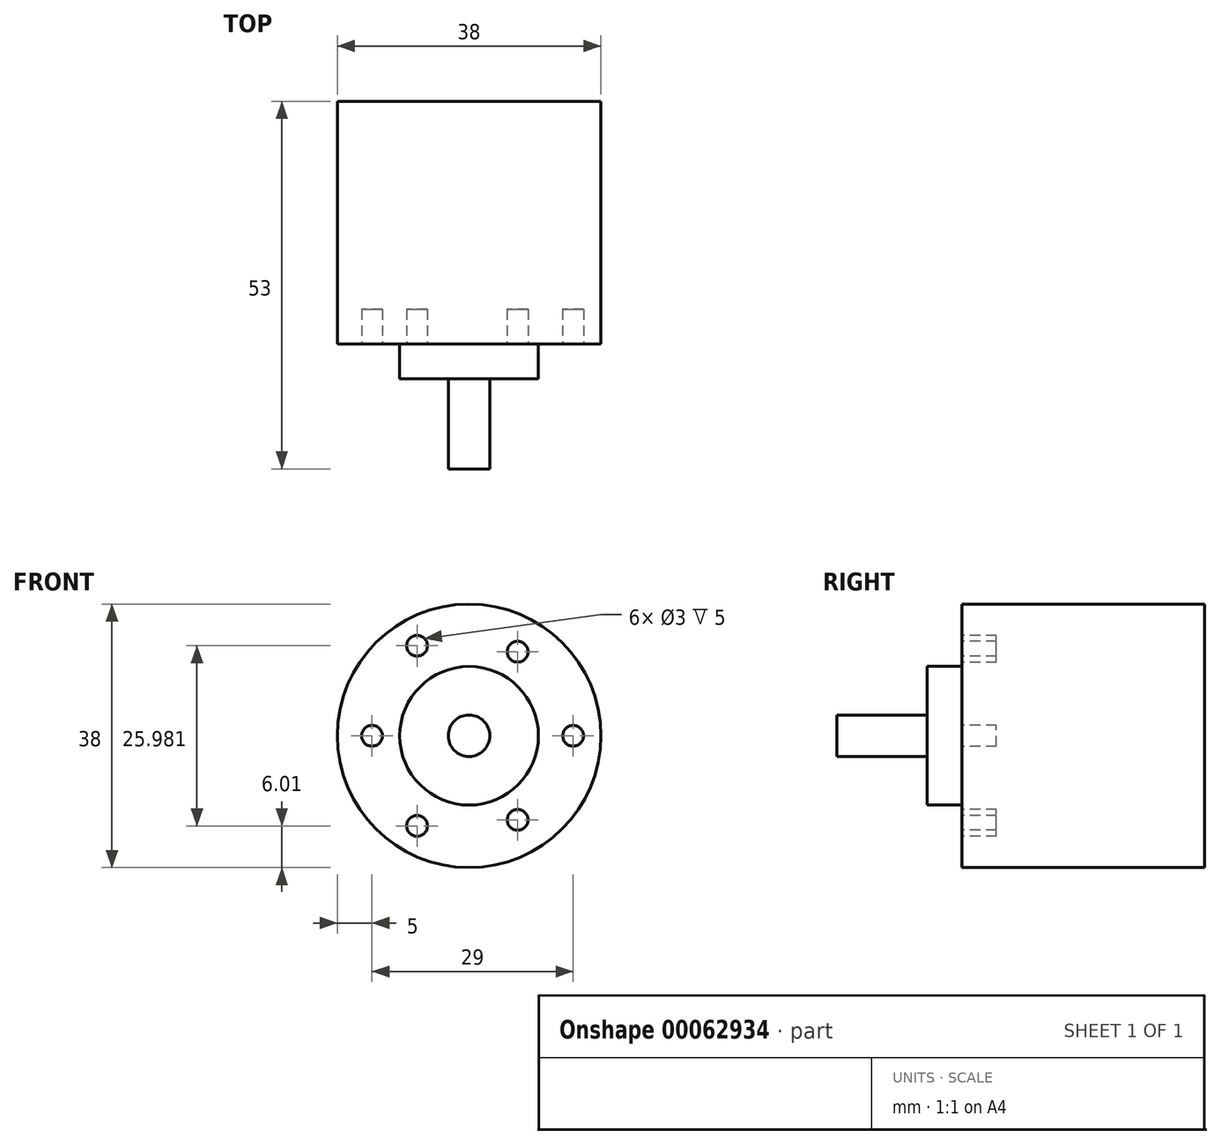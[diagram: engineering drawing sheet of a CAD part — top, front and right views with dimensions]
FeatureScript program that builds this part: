
annotation { "Feature Type Name" : "Feature", "Feature Type Description" : "" }
export const myFeature = defineFeature(function(context is Context, id is Id, definition is map)
    precondition{}
    {
        {
            var Q0;
            Q0=qCreatedBy(makeId("Front.planeOp"),FACE);
            var sketch = newSketch(context, id + "F0", { "sketchPlane" : qUnion([Q0])});
            skCircle(sketch, "E0", {"center": v(0, 0) * mm, "radius": 19 * mm});
            skSolve(sketch);
        }
        {
            var Q0;
            Q0 = qSketchRegion(id + "F0", true);
            extrude(context, id + "F1", {"entities" : qUnion([Q0]), "depth" : 35 * mm});
        }
        {
            var Q0;
            Q0=makeQuery(id+"F1.opExtrude","CAP_FACE",FACE,{"disambiguationData":[OSD([sQuery(id+"F0.wireOp",EDGE,"E0")])],"isStart":false});
            var sketch = newSketch(context, id + "F2", { "sketchPlane" : qUnion([Q0])});
            skCircle(sketch, "E1", {"center": v(0, 0) * mm, "radius": 10 * mm});
            skSolve(sketch);
        }
        {
            var Q0;
            Q0 = qSketchRegion(id + "F2", true);
            extrude(context, id + "F3", {"entities" : qUnion([Q0]), "operationType" : NewBodyOperationType.ADD, "depth" : 5 * mm});
        }
        {
            var Q0;
            Q0=makeQuery(id+"F3.opExtrude","CAP_FACE",FACE,{"disambiguationData":[OSD([sQuery(id+"F2.wireOp",EDGE,"E1")])],"isStart":false});
            var sketch = newSketch(context, id + "F4", { "sketchPlane" : qUnion([Q0])});
            skCircle(sketch, "E2", {"center": v(0, 0) * mm, "radius": 3 * mm});
            skSolve(sketch);
        }
        {
            var Q0;
            Q0 = qSketchRegion(id + "F4", true);
            extrude(context, id + "F5", {"entities" : qUnion([Q0]), "operationType" : NewBodyOperationType.ADD, "depth" : 13 * mm});
        }
        {
            var Q0;
            Q0=makeQuery(id+"F1.opExtrude","CAP_FACE",FACE,{"disambiguationData":[OSD([sQuery(id+"F0.wireOp",EDGE,"E0")])],"isStart":false});
            var sketch = newSketch(context, id + "F6", { "sketchPlane" : qUnion([Q0])});
            skCircle(sketch, "E3", {"center": v(0, 0) * mm, "radius": 15 * mm, "construction": true});
            skCircle(sketch, "E4", {"center": v(0, 0) * mm, "radius": 14 * mm, "construction": true});
            skLineSegment(sketch, "E5.0", {"start": v(15, 0) * mm, "end": v(7.5, -13) * mm, "construction": true});
            skLineSegment(sketch, "E5.1", {"start": v(7.5, -13) * mm, "end": v(-7.5, -13) * mm, "construction": true});
            skLineSegment(sketch, "E5.2", {"start": v(-7.5, -13) * mm, "end": v(-15, 0) * mm, "construction": true});
            skLineSegment(sketch, "E5.3", {"start": v(-15, 0) * mm, "end": v(-7.5, 13) * mm, "construction": true});
            skLineSegment(sketch, "E5.4", {"start": v(-7.5, 13) * mm, "end": v(7.5, 13) * mm, "construction": true});
            skLineSegment(sketch, "E5.5", {"start": v(7.5, 13) * mm, "end": v(15, 0) * mm, "construction": true});
            skLineSegment(sketch, "E6", {"start": v(0, 0) * mm, "end": v(-7.5, 13) * mm, "construction": true});
            skLineSegment(sketch, "E7", {"start": v(0, 0) * mm, "end": v(7.5, 13) * mm, "construction": true});
            skLineSegment(sketch, "E8", {"start": v(0, 0) * mm, "end": v(15, 0) * mm, "construction": true});
            skLineSegment(sketch, "E9", {"start": v(0, 0) * mm, "end": v(7.5, -13) * mm, "construction": true});
            skLineSegment(sketch, "E10", {"start": v(0, 0) * mm, "end": v(-7.5, -13) * mm, "construction": true});
            skLineSegment(sketch, "E11", {"start": v(0, 0) * mm, "end": v(-15, 0) * mm, "construction": true});
            skCircle(sketch, "E12", {"center": v(-7.5, 13) * mm, "radius": 1.5 * mm});
            skCircle(sketch, "E13", {"center": v(-14, 0) * mm, "radius": 1.5 * mm});
            skCircle(sketch, "E14", {"center": v(-7.5, -13) * mm, "radius": 1.5 * mm});
            skCircle(sketch, "E15", {"center": v(7, -12.12) * mm, "radius": 1.5 * mm});
            skCircle(sketch, "E16", {"center": v(15, 0) * mm, "radius": 1.5 * mm});
            skCircle(sketch, "E17", {"center": v(7, 12.12) * mm, "radius": 1.5 * mm});
            skSolve(sketch);
        }
        {
            var Q0;
            Q0 = qSketchRegion(id + "F6", true);
            extrude(context, id + "F7", {"entities" : qUnion([Q0]), "operationType" : NewBodyOperationType.REMOVE, "oppositeDirection" : true, "depth" : 5 * mm});
        }
    });
